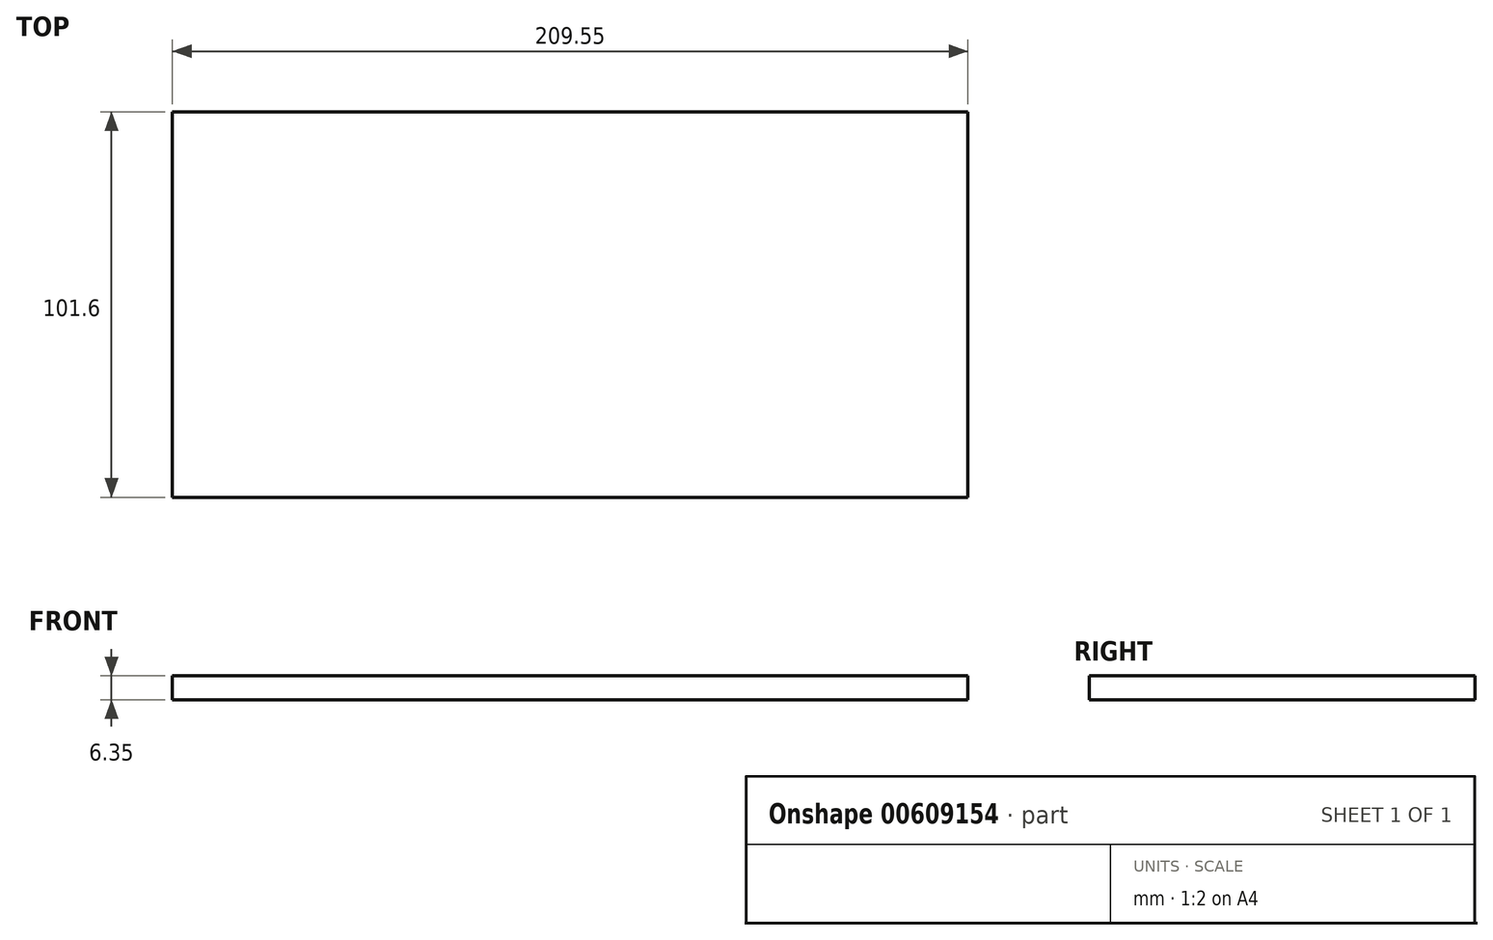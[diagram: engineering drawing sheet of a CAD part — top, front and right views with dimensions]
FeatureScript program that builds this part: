
annotation { "Feature Type Name" : "Feature", "Feature Type Description" : "" }
export const myFeature = defineFeature(function(context is Context, id is Id, definition is map)
    precondition{}
    {
        {
            var Q0;
            Q0=qCreatedBy(makeId("Top.planeOp"),FACE);
            var sketch = newSketch(context, id + "F0", { "sketchPlane" : qUnion([Q0])});
            skLineSegment(sketch, "E0.bottom", {"start": v(0, 0) * mm, "end": v(209.55, 0) * mm});
            skLineSegment(sketch, "E0.top", {"start": v(0, 101.6) * mm, "end": v(209.55, 101.6) * mm});
            skLineSegment(sketch, "E0.left", {"start": v(0, 0) * mm, "end": v(0, 101.6) * mm});
            skLineSegment(sketch, "E0.right", {"start": v(209.55, 0) * mm, "end": v(209.55, 101.6) * mm});
            skSolve(sketch);
        }
        {
            var Q0;
            Q0=makeQuery(id+"F0.imprint","IMPRINT",FACE,{"disambiguationData":[TD([[makeQuery(id+"F0.imprint","IMPRINT",EDGE,{"derivedFrom":sQuery(id+"F0.wireOp",EDGE,"E0.bottom")}),1.0]])]});
            extrude(context, id + "F1", {"entities" : qUnion([Q0]), "depth" : 6.35 * mm, "offsetDistance" : 25.4 * mm});
        }
    });
